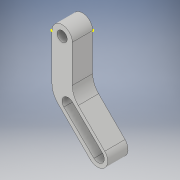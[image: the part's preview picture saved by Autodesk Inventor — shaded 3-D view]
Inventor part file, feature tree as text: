
AUTODESK INVENTOR PART (.ipt)
format: ipt  version: 2018.1 (Build 221171000, 171)  size: 134,656 bytes
history: native  units: in
note: dims shown in document units (in); Inventor stores cm internally (conversion verified against a paired STEP export)
features: sketch x6, other x3, extrude x1
ambient origin geometry x8: Origin, YZ Plane, XZ Plane, XY Plane, X Axis, Y Axis, Z Axis, Center Point
bodies: Solid1 (feature_tree)
feature tree (10):
  other  "Claw_design_gear_1.ipt"
  sketch  "Sketch6"
  sketch  "Sketch7"
  extrude  "Extrusion1"  Depth=0.886in TaperAngle=0.0deg
  other  "Solid1::Claw_design_gear_1.ipt"
  other  "TaggingFeature1"
  sketch  "Sketch2"  dims[d0=0.5906in d1=0.886in d2=0.0in]
  sketch  "Sketch3"
  sketch  "Sketch9"
  sketch  "Sketch11"
